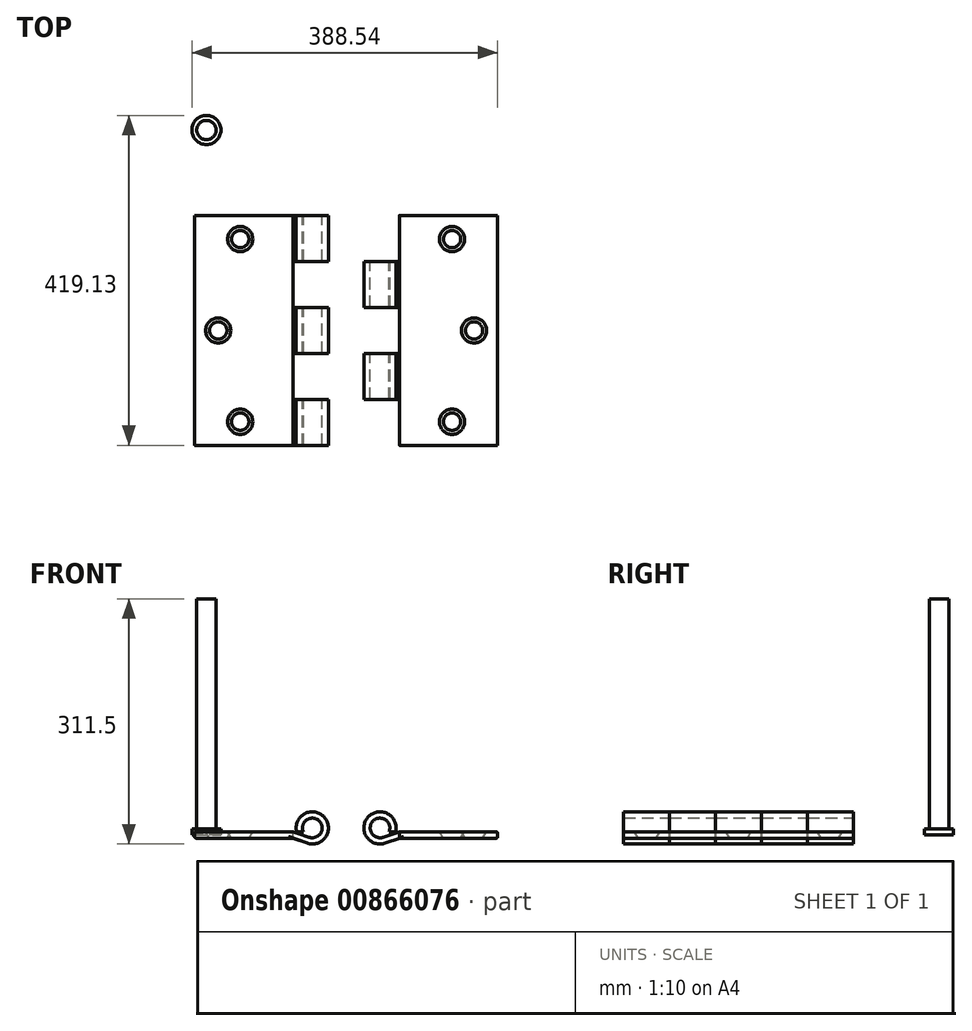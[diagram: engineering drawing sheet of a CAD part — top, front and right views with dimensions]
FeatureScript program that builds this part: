
annotation { "Feature Type Name" : "Feature", "Feature Type Description" : "" }
export const myFeature = defineFeature(function(context is Context, id is Id, definition is map)
    precondition{}
    {
        {
            var Q0;
            Q0=qCreatedBy(makeId("Front.planeOp"),FACE);
            var sketch = newSketch(context, id + "F0", { "sketchPlane" : qUnion([Q0])});
            skLineSegment(sketch, "E0.bottom", {"start": v(62.5, -4) * mm, "end": v(-62.5, -4) * mm});
            skLineSegment(sketch, "E0.top", {"start": v(62.5, 4) * mm, "end": v(-62.5, 4) * mm});
            skLineSegment(sketch, "E0.left", {"start": v(62.5, -4) * mm, "end": v(62.5, 4) * mm});
            skLineSegment(sketch, "E0.right", {"start": v(-62.5, -4) * mm, "end": v(-62.5, 4) * mm});
            skPoint(sketch, "E0.middle", {"position": v(0, 0) * mm});
            skArc(sketch, "E1", {"start": v(83.04, -2.86) * mm, "mid": v(95.44, 18.22) * mm, "end": v(75.54, 4) * mm});
            skArc(sketch, "E2", {"start": v(80.09, -10.3) * mm, "mid": v(102.18, 22.77) * mm, "end": v(67.12, 4) * mm});
            skLineSegment(sketch, "E3", {"start": v(87, 9) * mm, "end": v(87, -11.5) * mm, "construction": true});
            skLineSegment(sketch, "E4", {"start": v(62.5, -4) * mm, "end": v(80.09, -10.3) * mm});
            skLineSegment(sketch, "E5", {"start": v(67.12, 4) * mm, "end": v(87, 4) * mm});
            skLineSegment(sketch, "E6", {"start": v(87, 4) * mm, "end": v(87, 9) * mm});
            skLineSegment(sketch, "E7", {"start": v(62.5, 4) * mm, "end": v(83.04, -2.86) * mm});
            skSolve(sketch);
        }
        {
            var Q0;
            Q0=makeQuery(id+"F0.imprint","IMPRINT",FACE,{"disambiguationData":[TD([[makeQuery(id+"F0.imprint","IMPRINT",EDGE,{"derivedFrom":sQuery(id+"F0.wireOp",EDGE,"E0.bottom")}),-1.0]])]});
            var Q1;
            Q1=makeQuery(id+"F0.imprint","IMPRINT",FACE,{"disambiguationData":[TD([[makeQuery(id+"F0.imprint","IMPRINT",EDGE,{"derivedFrom":sQuery(id+"F0.wireOp",EDGE,"E0.left")}),-1.0]])]});
            extrude(context, id + "F1", {"entities" : qUnion([Q0, Q1]), "depth" : 292 * mm, "offsetDistance" : 25 * mm});
        }
        {
            var Q0;
            Q0=makeQuery(id+"F1.opExtrude","SWEPT_FACE",FACE,{"disambiguationData":[OSD([sQuery(id+"F0.wireOp",EDGE,"E0.top")])]});
            var sketch = newSketch(context, id + "F2", { "sketchPlane" : qUnion([Q0])});
            skLineSegment(sketch, "E8", {"start": v(-62.5, -262) * mm, "end": v(-62.5, -146) * mm, "construction": true});
            skLineSegment(sketch, "E9", {"start": v(-62.5, -146) * mm, "end": v(-32.5, -146) * mm, "construction": true});
            skCircle(sketch, "E10", {"center": v(-32.5, -146) * mm, "radius": 16 * mm});
            skLineSegment(sketch, "E11", {"start": v(-62.5, -262) * mm, "end": v(-4.5, -262) * mm, "construction": true});
            skCircle(sketch, "E12", {"center": v(-4.5, -262) * mm, "radius": 16 * mm});
            skLineSegment(sketch, "E13", {"start": v(-62.5, -146) * mm, "end": v(-62.5, -30) * mm, "construction": true});
            skLineSegment(sketch, "E14", {"start": v(-62.5, -30) * mm, "end": v(-4.5, -30) * mm, "construction": true});
            skCircle(sketch, "E15", {"center": v(-4.5, -30) * mm, "radius": 16 * mm});
            skLineSegment(sketch, "E16", {"start": v(62.5, 0) * mm, "end": v(142.5, 0) * mm});
            skLineSegment(sketch, "E17", {"start": v(142.5, 0) * mm, "end": v(142.5, -58.4) * mm});
            skLineSegment(sketch, "E18", {"start": v(142.5, -58.4) * mm, "end": v(62.5, -58.4) * mm});
            skLineSegment(sketch, "E19", {"start": v(142.5, -58.4) * mm, "end": v(142.5, -116.8) * mm});
            skLineSegment(sketch, "E20", {"start": v(142.5, -116.8) * mm, "end": v(62.5, -116.8) * mm});
            skLineSegment(sketch, "E21", {"start": v(142.5, -116.8) * mm, "end": v(142.5, -175.2) * mm});
            skLineSegment(sketch, "E22", {"start": v(142.5, -175.2) * mm, "end": v(62.5, -175.2) * mm});
            skLineSegment(sketch, "E23", {"start": v(142.5, -175.2) * mm, "end": v(142.5, -233.6) * mm});
            skLineSegment(sketch, "E24", {"start": v(142.5, -233.6) * mm, "end": v(62.5, -233.6) * mm});
            skLineSegment(sketch, "E25", {"start": v(142.5, -233.6) * mm, "end": v(142.5, -292) * mm});
            skLineSegment(sketch, "E26", {"start": v(142.5, -292) * mm, "end": v(62.5, -292) * mm});
            skSolve(sketch);
        }
        {
            var Q0;
            Q0=makeQuery(id+"F1.opExtrude","SWEPT_FACE",FACE,{"disambiguationData":[OSD([sQuery(id+"F0.wireOp",EDGE,"E0.bottom")])]});
            var sketch = newSketch(context, id + "F3", { "sketchPlane" : qUnion([Q0])});
            skCircle(sketch, "E27", {"center": v(-4.5, 262) * mm, "radius": 11 * mm});
            skCircle(sketch, "E28", {"center": v(-32.5, 146) * mm, "radius": 11 * mm});
            skCircle(sketch, "E29", {"center": v(-4.5, 30) * mm, "radius": 11 * mm});
            skSolve(sketch);
        }
        {
            var Q1;
            Q1=makeQuery(id+"F3.imprint","IMPRINT",FACE,{"disambiguationData":[TD([[makeQuery(id+"F3.imprint","IMPRINT",EDGE,{"derivedFrom":sQuery(id+"F3.wireOp",EDGE,"E28")}),1.0]])]});
            var Q2;
            Q2=makeQuery(id+"F2.imprint","IMPRINT",FACE,{"disambiguationData":[TD([[makeQuery(id+"F2.imprint","IMPRINT",EDGE,{"derivedFrom":sQuery(id+"F2.wireOp",EDGE,"E10")}),1.0]])]});
            loft(context, id + "F4", {"operationType" : NewBodyOperationType.REMOVE, "sheetProfilesArray" : [{ "sheetProfileEntities" : qUnion([Q1]) }, { "sheetProfileEntities" : qUnion([Q2]) }]});
        }
        {
            var Q1;
            Q1=makeQuery(id+"F3.imprint","IMPRINT",FACE,{"disambiguationData":[TD([[makeQuery(id+"F3.imprint","IMPRINT",EDGE,{"derivedFrom":sQuery(id+"F3.wireOp",EDGE,"E27")}),1.0]])]});
            var Q2;
            Q2=makeQuery(id+"F2.imprint","IMPRINT",FACE,{"disambiguationData":[TD([[makeQuery(id+"F2.imprint","IMPRINT",EDGE,{"derivedFrom":sQuery(id+"F2.wireOp",EDGE,"E12")}),1.0]])]});
            loft(context, id + "F5", {"operationType" : NewBodyOperationType.REMOVE, "sheetProfilesArray" : [{ "sheetProfileEntities" : qUnion([Q1]) }, { "sheetProfileEntities" : qUnion([Q2]) }]});
        }
        {
            var Q1;
            Q1=makeQuery(id+"F3.imprint","IMPRINT",FACE,{"disambiguationData":[TD([[makeQuery(id+"F3.imprint","IMPRINT",EDGE,{"derivedFrom":sQuery(id+"F3.wireOp",EDGE,"E29")}),1.0]])]});
            var Q2;
            Q2=makeQuery(id+"F2.imprint","IMPRINT",FACE,{"disambiguationData":[TD([[makeQuery(id+"F2.imprint","IMPRINT",EDGE,{"derivedFrom":sQuery(id+"F2.wireOp",EDGE,"E15")}),1.0]])]});
            loft(context, id + "F6", {"operationType" : NewBodyOperationType.REMOVE, "sheetProfilesArray" : [{ "sheetProfileEntities" : qUnion([Q1]) }, { "sheetProfileEntities" : qUnion([Q2]) }]});
        }
        {
            var Q0;
            Q0=qCreatedBy(makeId("Right.planeOp"),FACE);
            cPlane(context, id + "F7", {"entities" : qUnion([Q0]), "cplaneType" : CPlaneType.OFFSET, "offset" : 130 * mm, "width" : 150 * mm, "height" : 150 * mm});
        }
        {
            var Q0;
            Q0=makeQuery(id+"F1.opExtrude","CAP_EDGE",EDGE,{"disambiguationData":[OSD([sQuery(id+"F0.wireOp",EDGE,"E0.top")])],"isStart":false});
            var Q1;
            Q1=makeQuery(id+"F1.opExtrude","CAP_EDGE",EDGE,{"disambiguationData":[OSD([sQuery(id+"F0.wireOp",EDGE,"E0.bottom")])],"isStart":false});
            var Q2;
            Q2=makeQuery(id+"F1.opExtrude","CAP_EDGE",EDGE,{"disambiguationData":[OSD([sQuery(id+"F0.wireOp",EDGE,"E0.top")])],"isStart":true});
            var Q3;
            Q3=makeQuery(id+"F1.opExtrude","CAP_EDGE",EDGE,{"disambiguationData":[OSD([sQuery(id+"F0.wireOp",EDGE,"E0.bottom")])],"isStart":true});
            var Q4;
            Q4=makeQuery(id+"F1.opExtrude","SWEPT_EDGE",EDGE,{"disambiguationData":[OSD([sQuery(id+"F0.wireOp",EDGE,"E0.top"),sQuery(id+"F0.wireOp",EDGE,"E0.right")])]});
            var Q5;
            Q5=makeQuery(id+"F1.opExtrude","SWEPT_EDGE",EDGE,{"disambiguationData":[OSD([sQuery(id+"F0.wireOp",EDGE,"E0.bottom"),sQuery(id+"F0.wireOp",EDGE,"E0.right")])]});
            fillet(context, id + "F8", {"entities" : qUnion([Q0, Q1, Q2, Q3, Q4, Q5]), "radius" : 2 * mm, "tangentPropagation" : true, "allowEdgeOverflow" : false});
        }
        {
            var Q0;
            Q0=makeQuery(id+"F1.opExtrude","SWEPT_BODY",BODY,{"disambiguationData":[OSD([sQuery(id+"F0.wireOp",EDGE,"E0.bottom"),sQuery(id+"F0.wireOp",EDGE,"E0.top"),sQuery(id+"F0.wireOp",EDGE,"E0.right"),sQuery(id+"F0.wireOp",EDGE,"E1"),sQuery(id+"F0.wireOp",EDGE,"E2"),sQuery(id+"F0.wireOp",EDGE,"E4"),sQuery(id+"F0.wireOp",EDGE,"E5"),sQuery(id+"F0.wireOp",EDGE,"E7")])]});
            var Q1;
            Q1=qCreatedBy(id+"F7.planeOp",FACE);
            mirror(context, id + "F9", {"entities" : qUnion([Q0]), "mirrorPlane" : qUnion([Q1])});
        }
        {
            var Q0;
            {var subQ0=sQuery(id+"F2.wireOp",EDGE,"E18");Q0=makeQuery(id+"F2.imprint","IMPRINT",FACE,{"disambiguationData":[TD([[makeQuery(id+"F2.imprint","IMPRINT",EDGE,{"derivedFrom":subQ0}),1.0]])]});}
            var Q1;
            {var subQ0=sQuery(id+"F2.wireOp",EDGE,"E22");Q1=makeQuery(id+"F2.imprint","IMPRINT",FACE,{"disambiguationData":[TD([[makeQuery(id+"F2.imprint","IMPRINT",EDGE,{"derivedFrom":subQ0}),1.0]])]});}
            extrude(context, id + "F10", {"entities" : qUnion([Q0, Q1]), "operationType" : NewBodyOperationType.REMOVE, "endBound" : BoundingType.SYMMETRIC, "oppositeDirection" : true, "depth" : 100 * mm, "offsetDistance" : 25 * mm});
        }
        {
            var Q0;
            Q0=makeQuery(id+"F9.opPattern","COPY",FACE,{"derivedFrom":makeQuery(id+"F1.opExtrude","SWEPT_FACE",FACE,{"disambiguationData":[OSD([sQuery(id+"F0.wireOp",EDGE,"E0.top")])]}),"instanceName":"1"});
            var sketch = newSketch(context, id + "F11", { "sketchPlane" : qUnion([Q0])});
            skLineSegment(sketch, "E30", {"start": v(197.5, 0) * mm, "end": v(132.5, 0) * mm});
            skLineSegment(sketch, "E31", {"start": v(132.5, 0) * mm, "end": v(132.5, -58.4) * mm});
            skLineSegment(sketch, "E32", {"start": v(132.5, -58.4) * mm, "end": v(197.5, -58.4) * mm});
            skLineSegment(sketch, "E33", {"start": v(132.5, -58.4) * mm, "end": v(132.5, -116.8) * mm});
            skLineSegment(sketch, "E34", {"start": v(132.5, -116.8) * mm, "end": v(197.5, -116.8) * mm});
            skLineSegment(sketch, "E35", {"start": v(132.5, -116.8) * mm, "end": v(132.5, -175.2) * mm});
            skLineSegment(sketch, "E36", {"start": v(132.5, -175.2) * mm, "end": v(197.5, -175.2) * mm});
            skLineSegment(sketch, "E37", {"start": v(132.5, -175.2) * mm, "end": v(132.5, -233.6) * mm});
            skLineSegment(sketch, "E38", {"start": v(132.5, -233.6) * mm, "end": v(197.5, -233.6) * mm});
            skLineSegment(sketch, "E39", {"start": v(132.5, -233.6) * mm, "end": v(132.5, -292) * mm});
            skLineSegment(sketch, "E40", {"start": v(132.5, -292) * mm, "end": v(197.5, -292) * mm});
            skLineSegment(sketch, "E41", {"start": v(197.5, -290) * mm, "end": v(197.5, -292) * mm, "construction": true});
            skLineSegment(sketch, "E42", {"start": v(197.5, 0) * mm, "end": v(197.5, -2) * mm});
            skLineSegment(sketch, "E43", {"start": v(197.5, -292) * mm, "end": v(197.5, -290) * mm});
            skSolve(sketch);
        }
        {
            var Q0;
            {var subQ3=sQuery(id+"F11.wireOp",EDGE,"E38");Q0=makeQuery(id+"F11.imprint","IMPRINT",FACE,{"disambiguationData":[TD([[makeQuery(id+"F11.imprint","IMPRINT",EDGE,{"derivedFrom":subQ3}),-1.0]])]});}
            var Q1;
            {var subQ0=sQuery(id+"F11.wireOp",EDGE,"E34");Q1=makeQuery(id+"F11.imprint","IMPRINT",FACE,{"disambiguationData":[TD([[makeQuery(id+"F11.imprint","IMPRINT",EDGE,{"derivedFrom":subQ0}),-1.0]])]});}
            var Q2;
            Q2=makeQuery(id+"F11.imprint","IMPRINT",FACE,{"disambiguationData":[TD([[makeQuery(id+"F11.imprint","IMPRINT",EDGE,{"derivedFrom":sQuery(id+"F11.wireOp",EDGE,"E30")}),1.0]])]});
            extrude(context, id + "F12", {"entities" : qUnion([Q0, Q1, Q2]), "operationType" : NewBodyOperationType.REMOVE, "endBound" : BoundingType.SYMMETRIC, "oppositeDirection" : true, "depth" : 125 * mm, "offsetDistance" : 25 * mm});
        }
        {
            var Q0;
            Q0=qCreatedBy(makeId("Top.planeOp"),FACE);
            var sketch = newSketch(context, id + "F13", { "sketchPlane" : qUnion([Q0])});
            skCircle(sketch, "E44", {"center": v(-47.54, 108.63) * mm, "radius": 18.5 * mm});
            skSolve(sketch);
        }
        {
            var Q0;
            Q0=makeQuery(id+"F13.imprint","IMPRINT",FACE,{"disambiguationData":[TD([[makeQuery(id+"F13.imprint","IMPRINT",EDGE,{"derivedFrom":sQuery(id+"F13.wireOp",EDGE,"E44")}),1.0]])]});
            extrude(context, id + "F14", {"entities" : qUnion([Q0]), "depth" : 8 * mm, "offsetDistance" : 25 * mm});
        }
        {
            var Q0;
            Q0=makeQuery(id+"F14.opExtrude","CAP_FACE",FACE,{"disambiguationData":[OSD([sQuery(id+"F13.wireOp",EDGE,"E44")])],"isStart":false});
            var sketch = newSketch(context, id + "F15", { "sketchPlane" : qUnion([Q0])});
            skCircle(sketch, "E45", {"center": v(-47.54, 108.63) * mm, "radius": 12.25 * mm});
            skSolve(sketch);
        }
        {
            var Q0;
            Q0 = qSketchRegion(id + "F15", true);
            extrude(context, id + "F16", {"entities" : qUnion([Q0]), "operationType" : NewBodyOperationType.ADD, "depth" : 292 * mm, "offsetDistance" : 25 * mm});
        }
    });
